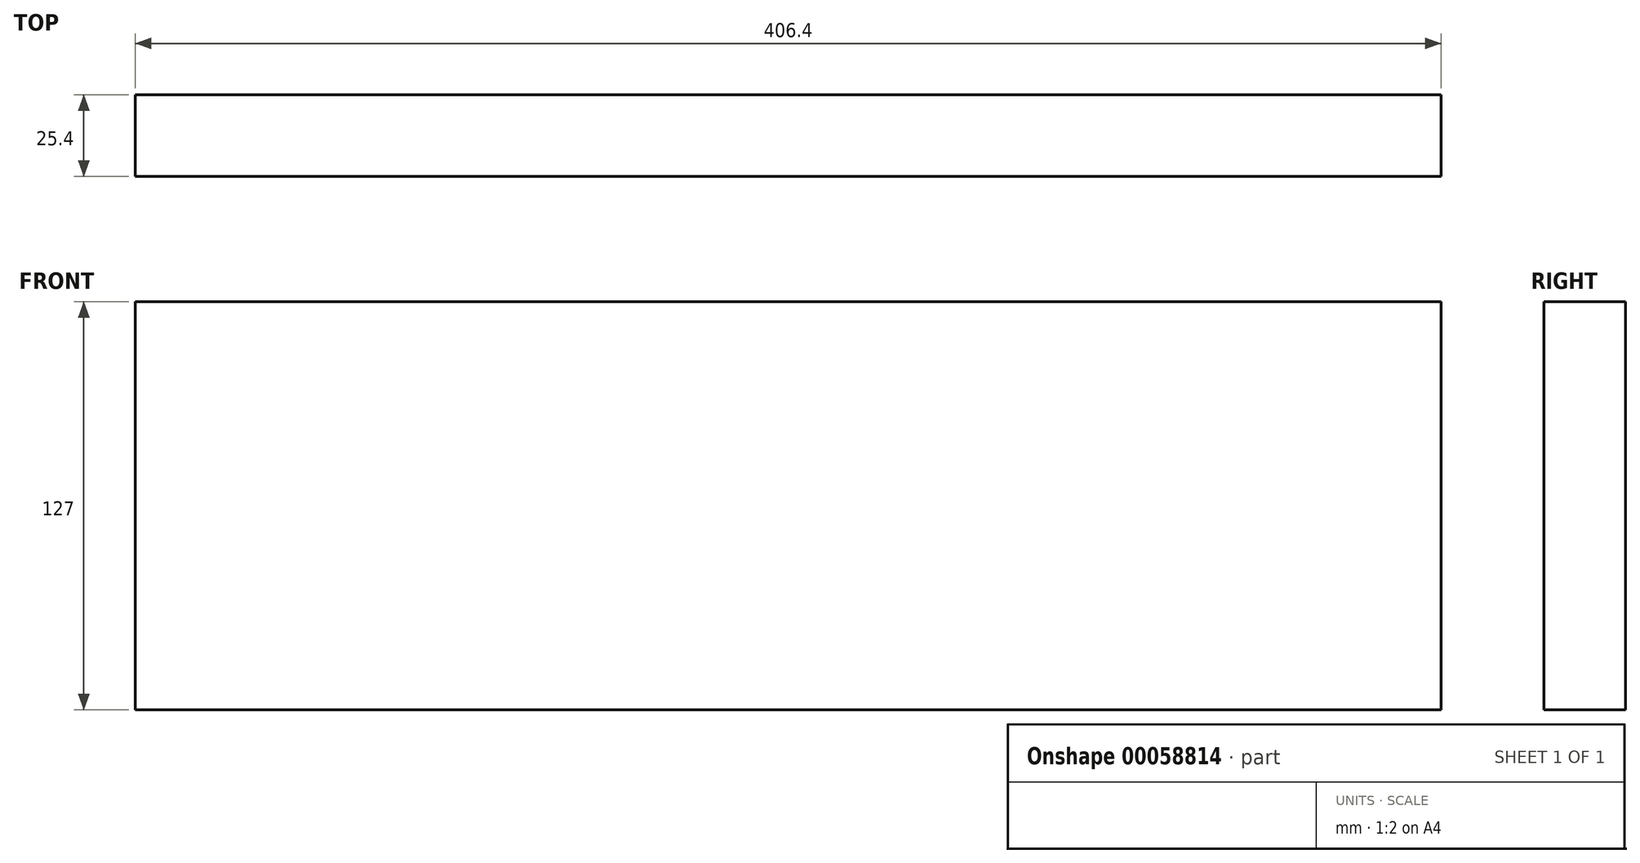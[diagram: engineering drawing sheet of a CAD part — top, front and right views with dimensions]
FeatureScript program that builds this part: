
annotation { "Feature Type Name" : "Feature", "Feature Type Description" : "" }
export const myFeature = defineFeature(function(context is Context, id is Id, definition is map)
    precondition{}
    {
        {
            var Q0;
            Q0=qCreatedBy(makeId("Front.planeOp"),FACE);
            var sketch = newSketch(context, id + "F0", { "sketchPlane" : qUnion([Q0])});
            skLineSegment(sketch, "E0.bottom", {"start": v(-406.4, 127) * mm, "end": v(0, 127) * mm});
            skLineSegment(sketch, "E0.top", {"start": v(-406.4, 0) * mm, "end": v(0, 0) * mm});
            skLineSegment(sketch, "E0.left", {"start": v(-406.4, 127) * mm, "end": v(-406.4, 0) * mm});
            skLineSegment(sketch, "E0.right", {"start": v(0, 127) * mm, "end": v(0, 0) * mm});
            skSolve(sketch);
        }
        {
            var Q0;
            Q0=makeQuery(id+"F0.imprint","IMPRINT",FACE,{"disambiguationData":[TD([[makeQuery(id+"F0.imprint","IMPRINT",EDGE,{"derivedFrom":sQuery(id+"F0.wireOp",EDGE,"E0.bottom")}),-1.0]])]});
            extrude(context, id + "F1", {"entities" : qUnion([Q0]), "depth" : 25.4 * mm});
        }
    });
